# Revit family: Hydraulic Buffer with Spring v2
name_source: partatom
category: Mechanical Equipment
units: mm (PartAtom-declared; Revit-internal decimal feet)

## family parameters
Always vertical = Yes
Cut with Voids When Loaded = No
Maintain Annotation Orientation = No
OmniClass Number = 23.75.00.00
OmniClass Title = Climate Control (HVAC)
Part Type = Normal
Room Calculation Point = No
Round Connector Dimension = Use Diameter
Shared = No
Work Plane-Based = No

## types (3) — shared parameters
Cylinder Diameter = 108 mm  [stored 0.354331 ft]
LiftBuffer_FixedToCar = Yes
Mounting plate Length = 200 mm  [stored 0.656168 ft]
Mounting plate height = 20 mm  [stored 0.0656168 ft]
Mounting plate width = 150 mm
Stroke Diameter = 75 mm
zero-valued in all types: Default Elevation

## per-type parameters (varying)
| type | Buffer Height | Cylinder Height | LiftBuffer_ImpactMassRange | LiftBuffer_RatedSpeed | LiftBuffer_Stroke |
| YHC175/A | 580 mm  [stored 1.90289 ft] | 290 mm  [stored 0.951444 ft] | 0 | 0.0 m/s | 0 |
| YHC275/A | 810 mm | 385 mm | 3000 | 2.0 m/s | 100 |
| YHC206 | 673 mm  [stored 2.20801 ft] | 337 mm | 0 | 0.0 m/s | 0 |

note: [stored X ft] marks values corroborated as IEEE doubles in the binary element streams (Revit-internal decimal feet)

## geometry (parser evidence)
native form markers: Sweep x3
no freeform markers — native parametric forms only
